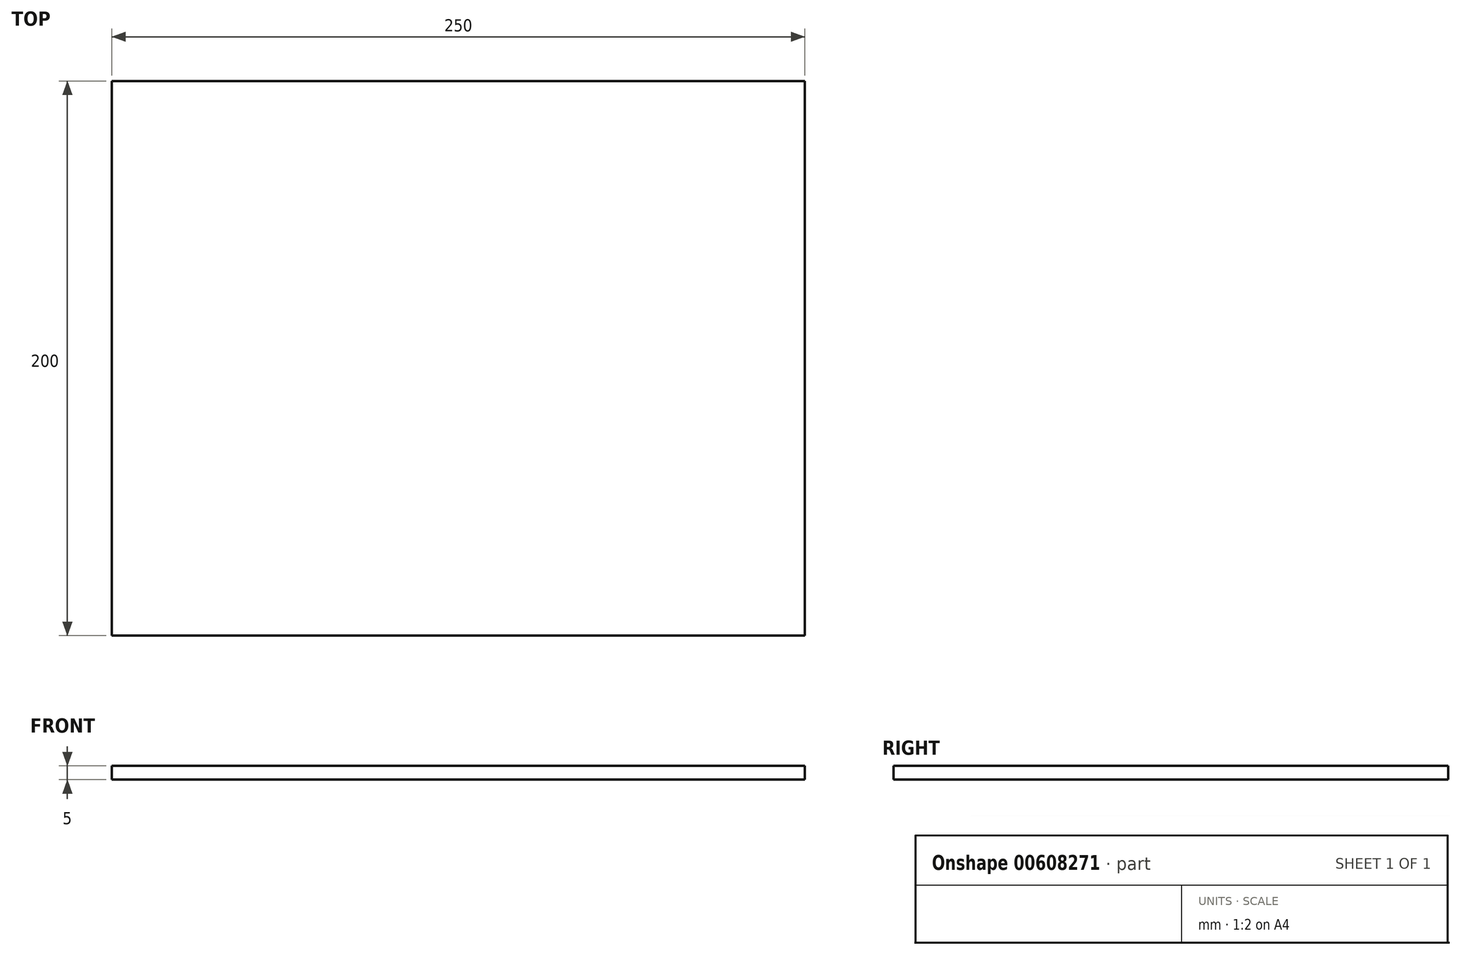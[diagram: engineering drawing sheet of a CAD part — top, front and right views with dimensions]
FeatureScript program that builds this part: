
annotation { "Feature Type Name" : "Feature", "Feature Type Description" : "" }
export const myFeature = defineFeature(function(context is Context, id is Id, definition is map)
    precondition{}
    {
        {
            var Q0;
            Q0=qCreatedBy(makeId("Top.planeOp"),FACE);
            var sketch = newSketch(context, id + "F0", { "sketchPlane" : qUnion([Q0])});
            skLineSegment(sketch, "E0.bottom", {"start": v(-125, 100) * mm, "end": v(125, 100) * mm});
            skLineSegment(sketch, "E0.top", {"start": v(-125, -100) * mm, "end": v(125, -100) * mm});
            skLineSegment(sketch, "E0.left", {"start": v(-125, 100) * mm, "end": v(-125, -100) * mm});
            skLineSegment(sketch, "E0.right", {"start": v(125, 100) * mm, "end": v(125, -100) * mm});
            skPoint(sketch, "E0.middle", {"position": v(0, 0) * mm});
            skSolve(sketch);
        }
        {
            var Q0;
            Q0 = qSketchRegion(id + "F0", true);
            extrude(context, id + "F1", {"entities" : qUnion([Q0]), "depth" : 5 * mm, "offsetDistance" : 25 * mm});
        }
    });
